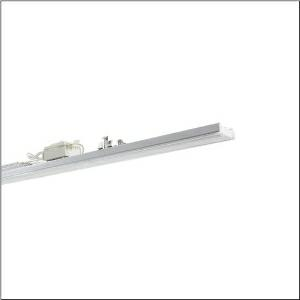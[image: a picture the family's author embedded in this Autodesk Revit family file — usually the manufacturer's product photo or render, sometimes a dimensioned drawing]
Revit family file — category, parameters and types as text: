
# Revit family: licross_r__21_recessed_mo_52tl12dv4fxg3s4_9313
name_source: partatom
category: Lighting Fixtures
units: mm (PartAtom-declared; Revit-internal decimal feet)

## family parameters
Cut with Voids When Loaded = No
Host = Face
Light Source = No
Part Type = Normal
Room Calculation Point = No
Round Connector Dimension = Use Diameter
Shared = No

## types (1)
- --- (1 x LED, 950 lm, 5.5 W, 4000K)
    Apparent Load = 6 VA
    CIE Flux Codes = 72 92 99 100 100
    Color Rendering = 80
    Color Temperature = 4000K
    Default Elevation = 1800 mm
    Description = Licross® 21 Recessed MO, luminaire insert, of sheet steel, galvanised, coil coated, white, length: 2.250mm, width: 66mm, height: 67mm, LED rated luminous flux: 15.420lm, light colour: 840, control gear: DALI 2, with plug, 6-pole, with phase selection, for trunking rail, 9 or 11-core, mains connection: 220..240V, AC, 50/60Hz, rated input power: 89W, for trunking rail, 9-/11-core, halogen-free wiring, for emergency light function, converter,control gear: single battery element, battery: LiFePO4, 9Ah, primary optical cover: cover, of PMMA, light emission: direct distribution, primary light characteristic: symmetric, protection rating (complete): IP40, insulation class (complete): insulation class I (protective earthing), certification: CE, UKCA, protection symbol: D if used in an environment without relevant dust loads with corresponding accessories, impact resistance: IK06, permissible ambient temperature for indoor applications: +5..+35°C, standard: EN 60598-2-22, LABS conformity tested according to VDMA 24364:2018-05, reducing of maximum allowable ambient temperature of 5°C with ceiling mounting, corresponds to IFS (International Featured Standards) requirements for safety and quality in the food industry, packaging unit: 1 piece
    Height = 58 mm
    Lamp = 1 x LED
    Lamp Light Flux = 950 lm
    Lamp Power = 5.5 W
    Lamp count = 1
    Length = 2250 mm
    Luminous efficacy = 173 lm/W
    Manufacturer = Siteco
    ModVariant = No
    Model = 52TL12DV4FXG3S4
    Mounting Place = Ceiling
    Mounting Type = Pendant
    Number of Poles = 1
    OnlyDefault = Yes
    Power Factor = 1
    Product Name = Licross® 21 Recessed MO
    Product group = luminaire insert
    ProductGroupID = 902
    Protection Class = Protection class I
    Protection Degree = IP 40
    RLX_Detail_Level = 1
    RLX_Emergency_Light_Flux = 0 lm
    RLX_Emergency_Type = 0
    RLX_Emergency_Type_DB = No
    RlxData = <blob elided: 30005 chars, md5=77bf2e5c>
    Socket = socket
    Standby Power = 0 W
    System Light Flux = 950 lm
    System Power = 6 W
    Type Comments = : emergency light operation: 3 h
    Type Image = l_1296930.jpg
    URL = http://relux.com
    VarID = @adj_110064
    Voltage = 0 V
    Weight = 0.00 kg
    Width = 66 mm

## geometry (parser evidence)
native form markers: Blend x4, Sweep x8
no freeform markers — native parametric forms only
